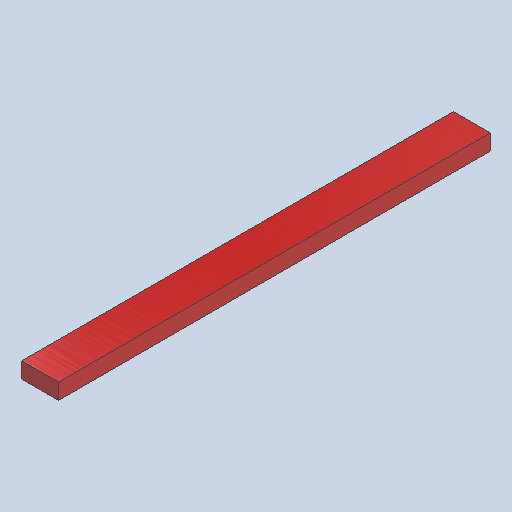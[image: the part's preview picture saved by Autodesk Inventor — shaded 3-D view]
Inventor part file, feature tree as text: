
AUTODESK INVENTOR PART (.ipt)
format: ipt  version: 2025 (Build 290162000, 162)  size: 97,792 bytes
history: native  units: in
note: dims shown in document units (in); Inventor stores cm internally (conversion verified against a paired STEP export)
features: other x4, sketch x1, plane x1
ambient origin geometry x8: Origin, YZ Plane, XZ Plane, XY Plane, X Axis, Y Axis, Z Axis, Center Point
bodies: Solid1 (feature_tree)
feature tree (6):
  other  "3'5x2x4.ipt"
  other  "Solid1::3'5x2x4.ipt"
  other  "TaggingFeature1"
  sketch  "Sketch1"  dims[d0=0.3937in]
  plane  "Work Plane1"
  other  "Finish1"
